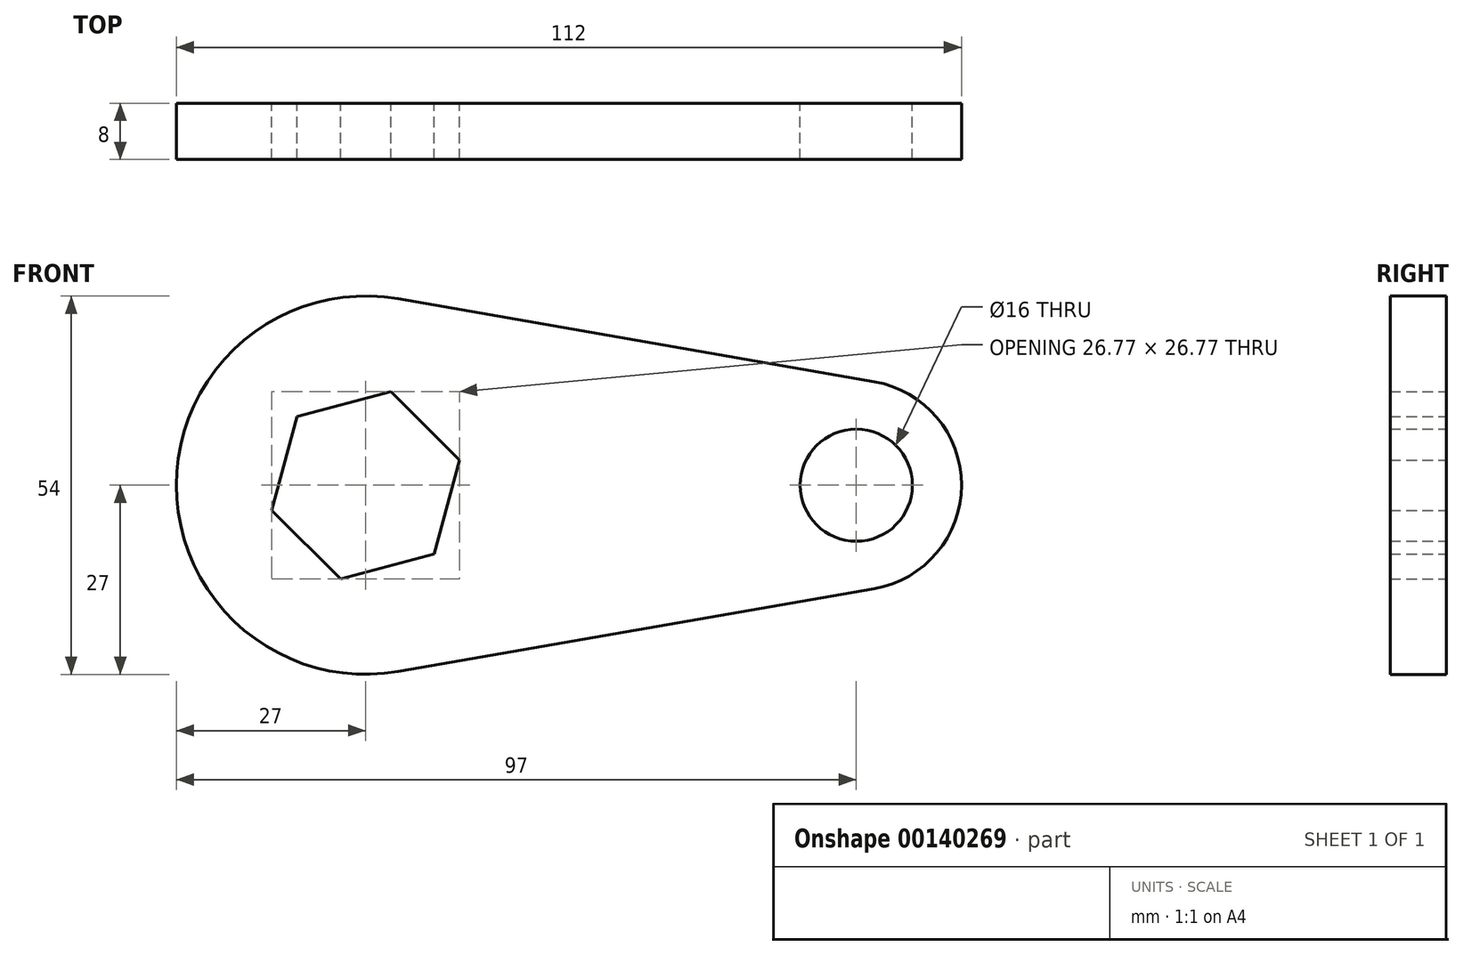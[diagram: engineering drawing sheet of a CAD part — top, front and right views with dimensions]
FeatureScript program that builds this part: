
annotation { "Feature Type Name" : "Feature", "Feature Type Description" : "" }
export const myFeature = defineFeature(function(context is Context, id is Id, definition is map)
    precondition{}
    {
        {
            var Q0;
            Q0=qCreatedBy(makeId("Front.planeOp"),FACE);
            var sketch = newSketch(context, id + "F0", { "sketchPlane" : qUnion([Q0])});
            skCircle(sketch, "E0.cCircle", {"center": v(0, 0) * mm, "radius": 12 * mm, "construction": true});
            skLineSegment(sketch, "E0.0", {"start": v(13.38, 3.59) * mm, "end": v(9.8, -9.8) * mm});
            skLineSegment(sketch, "E0.1", {"start": v(9.8, -9.8) * mm, "end": v(-3.59, -13.38) * mm});
            skLineSegment(sketch, "E0.2", {"start": v(-3.59, -13.38) * mm, "end": v(-13.38, -3.59) * mm});
            skLineSegment(sketch, "E0.3", {"start": v(-13.38, -3.59) * mm, "end": v(-9.8, 9.8) * mm});
            skLineSegment(sketch, "E0.4", {"start": v(-9.8, 9.8) * mm, "end": v(3.59, 13.38) * mm});
            skLineSegment(sketch, "E0.5", {"start": v(3.59, 13.38) * mm, "end": v(13.38, 3.59) * mm});
            skPoint(sketch, "E0.0.midPoint", {"position": v(11.6, -3.1) * mm});
            skCircle(sketch, "E1", {"center": v(70, 0) * mm, "radius": 8 * mm});
            skLineSegment(sketch, "E2", {"start": v(0, 0) * mm, "end": v(70, 0) * mm, "construction": true});
            skArc(sketch, "E3", {"start": v(4.63, 26.6) * mm, "mid": v(-27, 0) * mm, "end": v(4.63, -26.6) * mm});
            skArc(sketch, "E4", {"start": v(72.57, -14.78) * mm, "mid": v(85, 0) * mm, "end": v(72.57, 14.78) * mm});
            skLineSegment(sketch, "E5", {"start": v(4.63, -26.6) * mm, "end": v(72.57, -14.78) * mm});
            skLineSegment(sketch, "E6.MirrorCS", {"start": v(4.63, 26.6) * mm, "end": v(72.57, 14.78) * mm});
            skLineSegment(sketch, "E7", {"start": v(0, 40.5) * mm, "end": v(0, -45.47) * mm, "construction": true});
            skLineSegment(sketch, "E8", {"start": v(78, 0) * mm, "end": v(0, 0) * mm});
            skSolve(sketch);
        }
        {
            var Q0;
            {var subQ7=sQuery(id+"F0.wireOp",EDGE,"E0.1");Q0=makeQuery(id+"F0.imprint","IMPRINT",FACE,{"disambiguationData":[TD([[makeQuery(id+"F0.imprint","IMPRINT",EDGE,{"derivedFrom":subQ7}),1.0]])]});}
            extrude(context, id + "F1", {"entities" : qUnion([Q0]), "depth" : 8 * mm});
        }
    });
